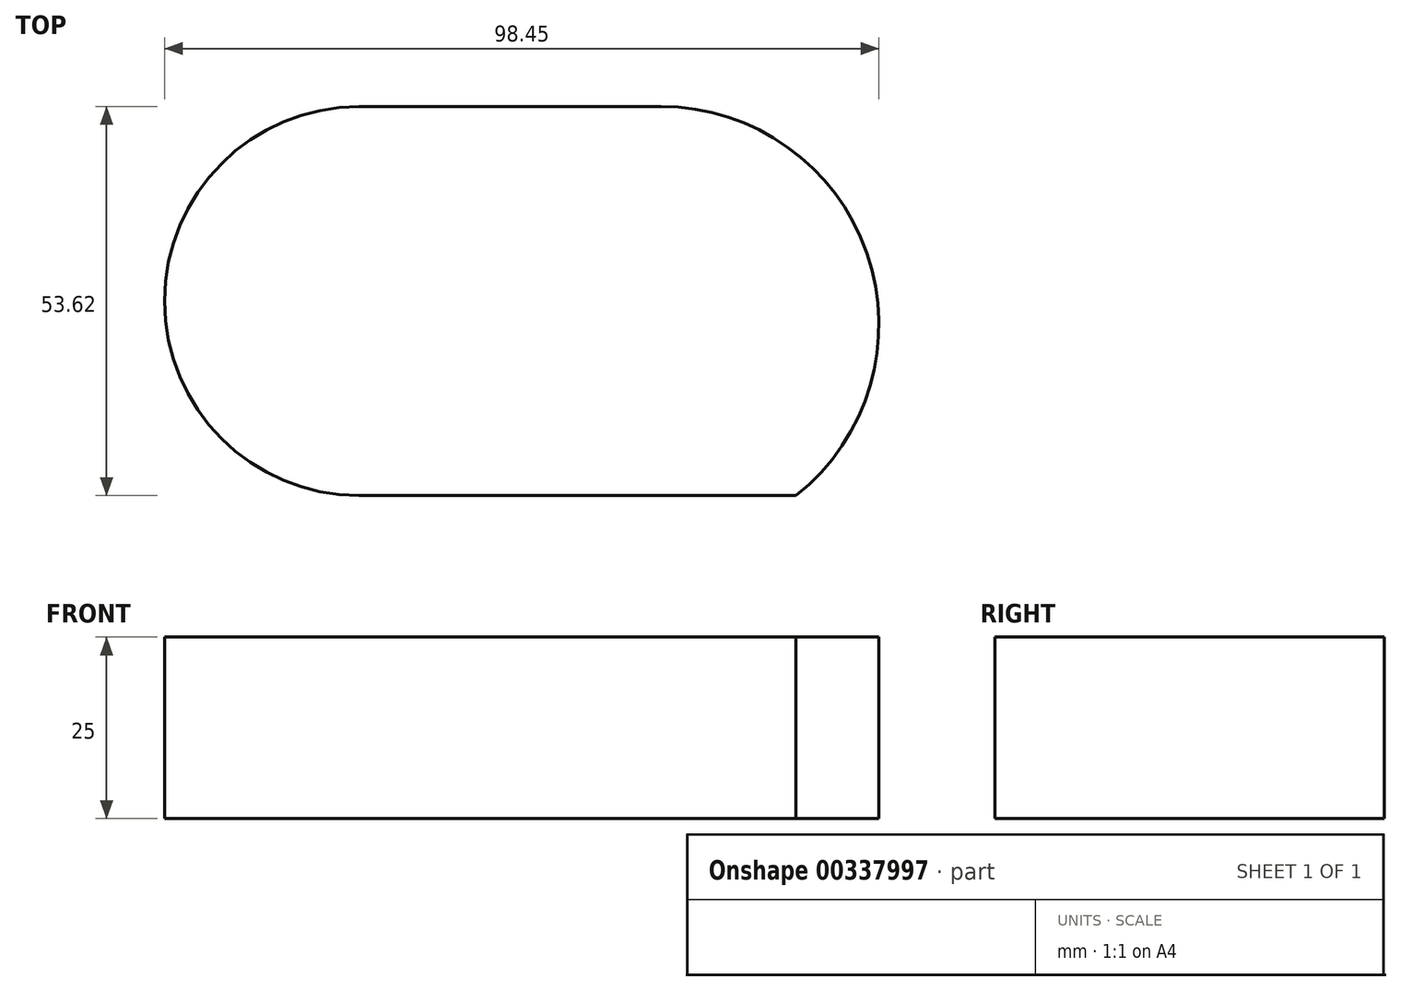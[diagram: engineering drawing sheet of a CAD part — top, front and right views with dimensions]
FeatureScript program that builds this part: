
annotation { "Feature Type Name" : "Feature", "Feature Type Description" : "" }
export const myFeature = defineFeature(function(context is Context, id is Id, definition is map)
    precondition{}
    {
        {
            var Q0;
            Q0=qCreatedBy(makeId("Top.planeOp"),FACE);
            var sketch = newSketch(context, id + "F0", { "sketchPlane" : qUnion([Q0])});
            skCircle(sketch, "E0", {"center": v(0, 0) * mm, "radius": 26.8 * mm});
            skLineSegment(sketch, "E1", {"start": v(0, -26.8) * mm, "end": v(60.2, -26.8) * mm});
            skLineSegment(sketch, "E2", {"start": v(0, 26.8) * mm, "end": v(41.6, 26.8) * mm});
            skArc(sketch, "E3", {"start": v(60.2, -26.8) * mm, "mid": v(69.98, 6.62) * mm, "end": v(41.6, 26.8) * mm});
            skSolve(sketch);
        }
        {
            var Q0;
            {var subQ0=sQuery(id+"F0.wireOp",EDGE,"E0");var subQ1=makeQuery(id+"F0.imprint","INTERSECT",VERTEX,{"derivedFrom":[subQ0,sQuery(id+"F0.wireOp",EDGE,"E1")]});Q0=makeQuery(id+"F0.imprint","IMPRINT",FACE,{"disambiguationData":[TD([[makeQuery(id+"F0.imprint","IMPRINT",EDGE,{"disambiguationData":[TD([[subQ1,1.0]])],"derivedFrom":subQ0}),1.0]])]});}
            var Q1;
            {var subQ0=sQuery(id+"F0.wireOp",EDGE,"E1");Q1=makeQuery(id+"F0.imprint","IMPRINT",FACE,{"disambiguationData":[TD([[makeQuery(id+"F0.imprint","IMPRINT",EDGE,{"derivedFrom":subQ0}),1.0]])]});}
            extrude(context, id + "F1", {"entities" : qUnion([Q0, Q1]), "depth" : 25 * mm});
        }
    });
